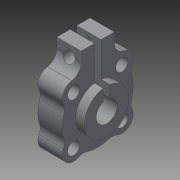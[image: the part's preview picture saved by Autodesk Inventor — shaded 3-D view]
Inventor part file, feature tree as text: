
AUTODESK INVENTOR PART (.ipt)
format: ipt  version: 2014 SP1 (Build 180222100, 222)  size: 252,928 bytes
history: native  units: in
note: dims shown in document units (in); Inventor stores cm internally (conversion verified against a paired STEP export)
features: extrude x3, sketch x3, thread x2, chamfer x1
ambient origin geometry x8: Origin, YZ Plane, XZ Plane, XY Plane, X Axis, Y Axis, Z Axis, Center Point
bodies: Solid1 (feature_tree)
feature tree (9):
  extrude  "Extrusion1"  Depth=0.77in
  extrude  "Extrusion2"  Depth=0.138in
  extrude  "Extrusion3"  Depth=0.275in
  thread  "Thread1"  [1 undecoded]
  thread  "Thread2"  [1 undecoded]
  chamfer  "Chamfer1"  Distance=0.0375in
  sketch  "Sketch1"  dims[d1=0.8in d4=0.77in]
  sketch  "Sketch2"  dims[d6=0.138in d7=0.138in]
  sketch  "Sketch3"  dims[d8=0.138in d9=0.138in d11=0.2362in d12=1.035in d16=0.0375in d17=0.038in d18=0.125in d19=0.125in d20=0.275in d21=0.0in d22=0.5in d23=0.1in d24=0.0in d25=0.138in d26=1.1625in d27=0.0in d28=1.0in d29=0.0in d30=1.0in d31=0.0in d32=0.01in d33=0.125in d34=45.0deg]
note: 2 required parameter values undecoded (feature->parameter linkage not recoverable at this tier; creation-order binding heuristic only, values carry confidence <= 0.55)
